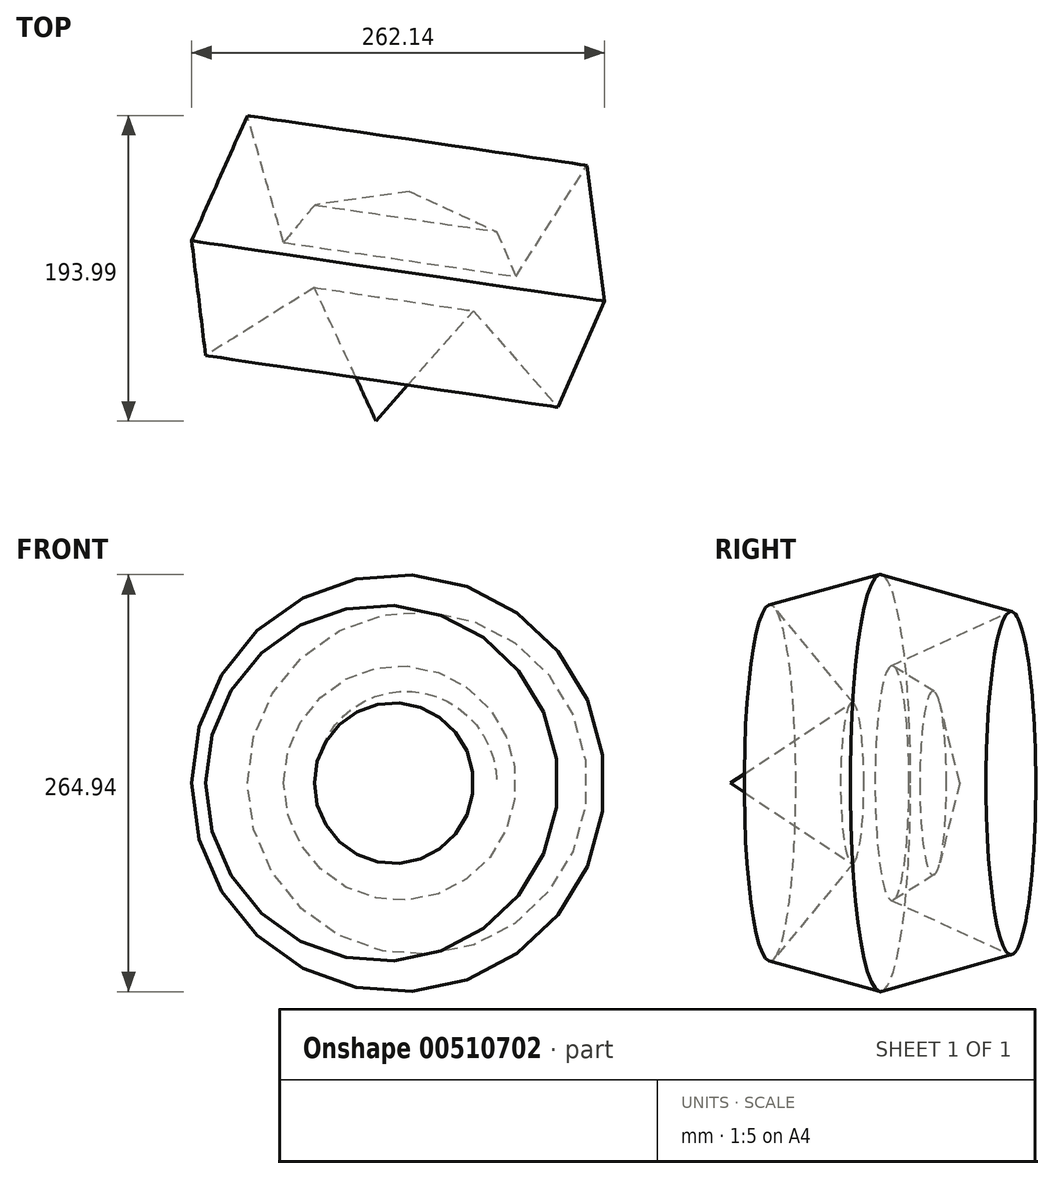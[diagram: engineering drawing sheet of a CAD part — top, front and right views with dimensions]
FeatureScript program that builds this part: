
annotation { "Feature Type Name" : "Feature", "Feature Type Description" : "" }
export const myFeature = defineFeature(function(context is Context, id is Id, definition is map)
    precondition{}
    {
        {
            var Q0;
            Q0=qCreatedBy(makeId("Top.planeOp"),FACE);
            var sketch = newSketch(context, id + "F0", { "sketchPlane" : qUnion([Q0])});
            skLineSegment(sketch, "E0", {"start": v(-67.42, 69.5) * mm, "end": v(-88.78, -76.3) * mm});
            skLineSegment(sketch, "E1", {"start": v(-88.78, -76.3) * mm, "end": v(-26.74, -6.11) * mm});
            skLineSegment(sketch, "E2", {"start": v(-27.08, -6.11) * mm, "end": v(26.83, -67.48) * mm});
            skLineSegment(sketch, "E3", {"start": v(26.83, -67.48) * mm, "end": v(56.33, 0) * mm});
            skLineSegment(sketch, "E4", {"start": v(56.33, -0.69) * mm, "end": v(45.14, 86.1) * mm});
            skLineSegment(sketch, "E5", {"start": v(45.14, 86.1) * mm, "end": v(0, 15.59) * mm});
            skLineSegment(sketch, "E6", {"start": v(0, 15.59) * mm, "end": v(-12.16, 44.07) * mm});
            skLineSegment(sketch, "E7", {"start": v(-12.16, 44.07) * mm, "end": v(-67.42, 69.5) * mm});
            skSolve(sketch);
        }
        {
            var Q0;
            {var subQ7=sQuery(id+"F0.wireOp",EDGE,"E0");Q0=makeQuery(id+"F0.imprint","IMPRINT",FACE,{"disambiguationData":[TD([[makeQuery(id+"F0.imprint","IMPRINT",EDGE,{"derivedFrom":subQ7}),1.0]])]});}
            var Q1;
            Q1=sQuery(id+"F0.wireOp",EDGE,"E0");
            revolve(context, id + "F1", {"entities" : qUnion([Q0]), "axis" : qUnion([Q1]), "revolveType" : RevolveType.FULL});
        }
    });
